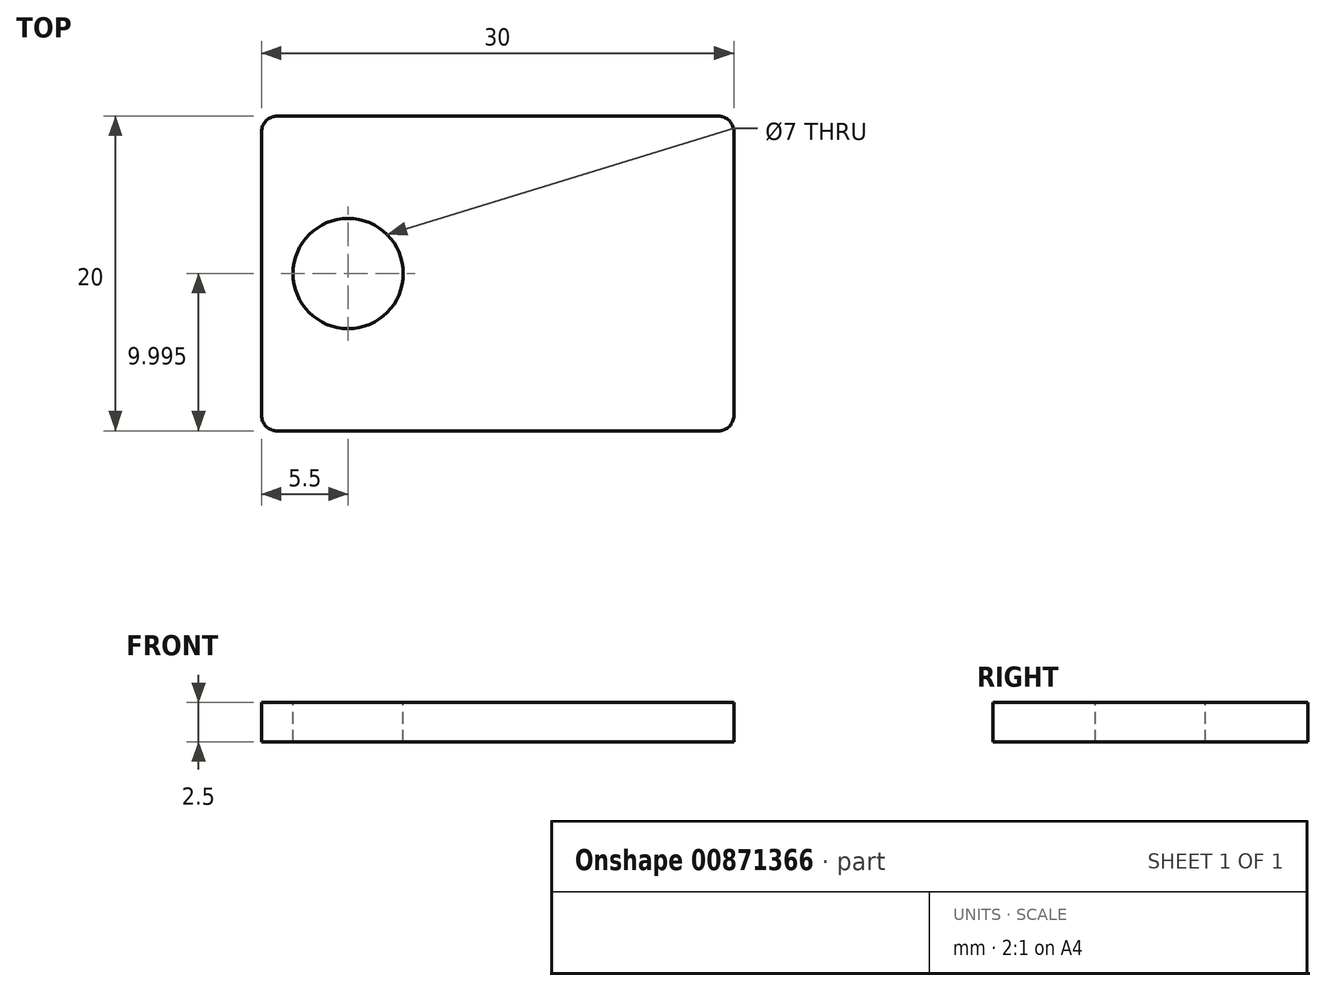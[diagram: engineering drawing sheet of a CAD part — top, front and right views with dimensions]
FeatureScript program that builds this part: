
annotation { "Feature Type Name" : "Feature", "Feature Type Description" : "" }
export const myFeature = defineFeature(function(context is Context, id is Id, definition is map)
    precondition{}
    {
        {
            var Q0;
            Q0=qCreatedBy(makeId("Top.planeOp"),FACE);
            var sketch = newSketch(context, id + "F0", { "sketchPlane" : qUnion([Q0])});
            skLineSegment(sketch, "E0.bottom", {"start": v(-9.16, 11.06) * mm, "end": v(20.84, 11.06) * mm});
            skLineSegment(sketch, "E0.top", {"start": v(-9.16, -8.94) * mm, "end": v(20.84, -8.94) * mm});
            skLineSegment(sketch, "E0.left", {"start": v(-9.16, 11.06) * mm, "end": v(-9.16, -8.94) * mm});
            skLineSegment(sketch, "E0.right", {"start": v(20.84, 11.06) * mm, "end": v(20.84, -8.94) * mm});
            skSolve(sketch);
        }
        {
            var Q0;
            Q0 = qSketchRegion(id + "F0", true);
            extrude(context, id + "F1", {"entities" : qUnion([Q0]), "depth" : 2.5 * mm, "offsetDistance" : 25 * mm});
        }
        {
            var Q0;
            Q0=makeQuery(id+"F1.opExtrude","SWEPT_EDGE",EDGE,{"disambiguationData":[OSD([sQuery(id+"F0.wireOp",EDGE,"E0.bottom"),sQuery(id+"F0.wireOp",EDGE,"E0.left")])]});
            fillet(context, id + "F2", {"entities" : qUnion([Q0]), "radius" : 1 * mm, "tangentPropagation" : true, "allowEdgeOverflow" : false});
        }
        {
            var Q0;
            Q0=makeQuery(id+"F1.opExtrude","SWEPT_EDGE",EDGE,{"disambiguationData":[OSD([sQuery(id+"F0.wireOp",EDGE,"E0.bottom"),sQuery(id+"F0.wireOp",EDGE,"E0.right")])]});
            var Q1;
            Q1=makeQuery(id+"F1.opExtrude","SWEPT_EDGE",EDGE,{"disambiguationData":[OSD([sQuery(id+"F0.wireOp",EDGE,"E0.top"),sQuery(id+"F0.wireOp",EDGE,"E0.right")])]});
            var Q2;
            Q2=makeQuery(id+"F1.opExtrude","SWEPT_EDGE",EDGE,{"disambiguationData":[OSD([sQuery(id+"F0.wireOp",EDGE,"E0.top"),sQuery(id+"F0.wireOp",EDGE,"E0.left")])]});
            fillet(context, id + "F3", {"entities" : qUnion([Q0, Q1, Q2]), "radius" : 1 * mm, "tangentPropagation" : true, "allowEdgeOverflow" : false});
        }
        {
            var Q0;
            Q0=makeQuery(id+"F1.opExtrude","CAP_FACE",FACE,{"disambiguationData":[OSD([sQuery(id+"F0.wireOp",EDGE,"E0.bottom"),sQuery(id+"F0.wireOp",EDGE,"E0.top"),sQuery(id+"F0.wireOp",EDGE,"E0.left"),sQuery(id+"F0.wireOp",EDGE,"E0.right")])],"isStart":false});
            var sketch = newSketch(context, id + "F4", { "sketchPlane" : qUnion([Q0])});
            skCircle(sketch, "E1", {"center": v(-3.66, 1.06) * mm, "radius": 3.5 * mm});
            skSolve(sketch);
        }
        {
            var Q0;
            Q0=makeQuery(id+"F4.imprint","IMPRINT",FACE,{"disambiguationData":[TD([[makeQuery(id+"F4.imprint","IMPRINT",EDGE,{"derivedFrom":sQuery(id+"F4.wireOp",EDGE,"E1")}),1.0]])]});
            extrude(context, id + "F5", {"entities" : qUnion([Q0]), "operationType" : NewBodyOperationType.REMOVE, "endBound" : BoundingType.THROUGH_ALL, "oppositeDirection" : true, "depth" : 25 * mm, "offsetDistance" : 25 * mm});
        }
    });
